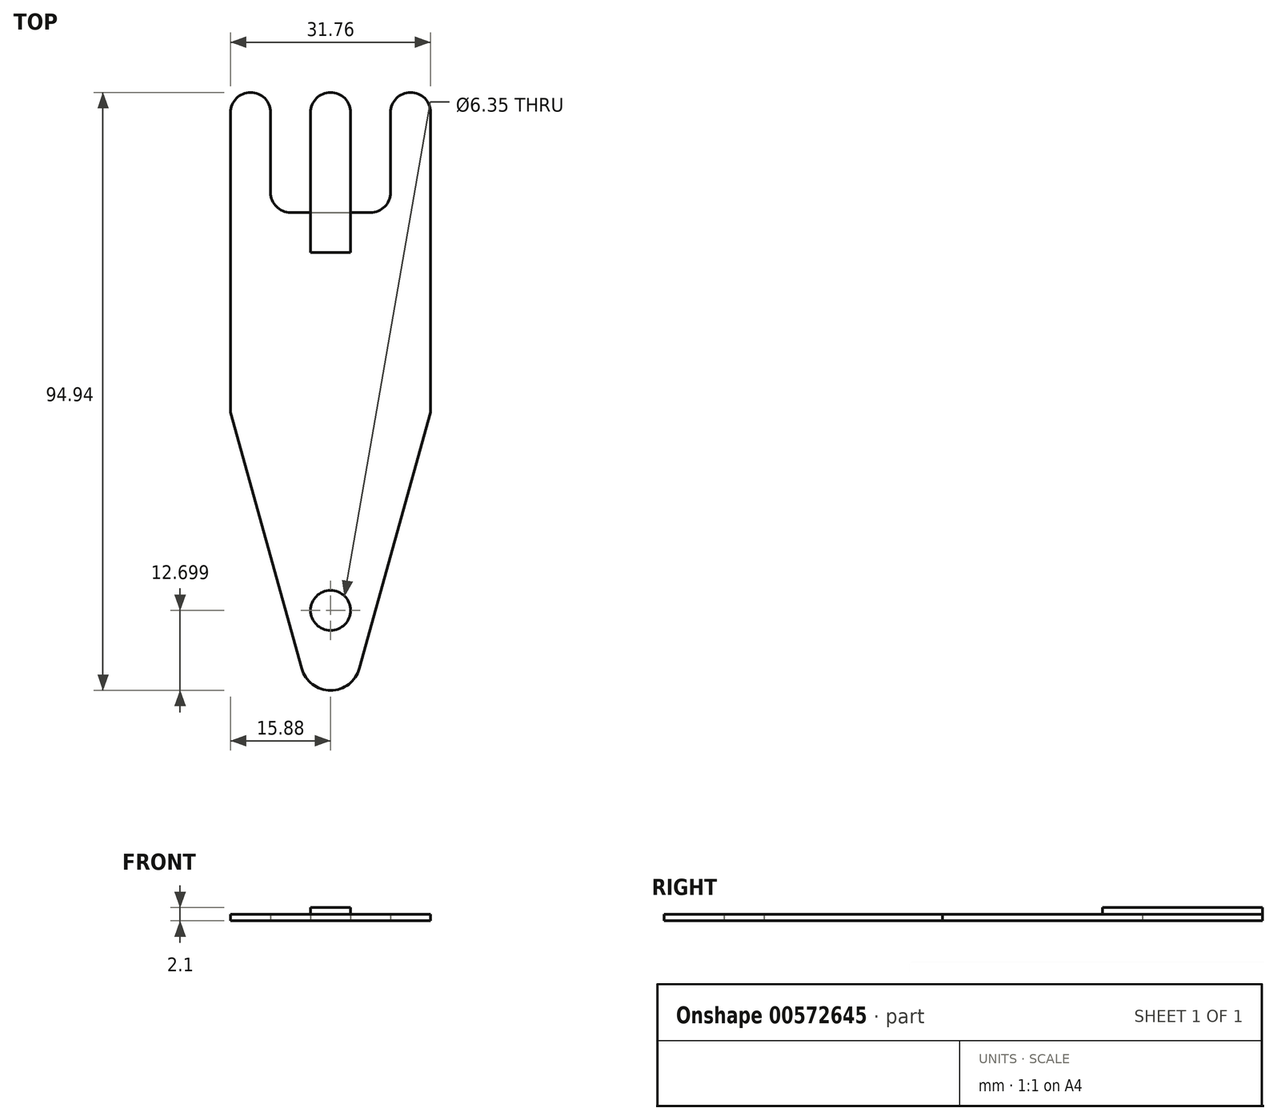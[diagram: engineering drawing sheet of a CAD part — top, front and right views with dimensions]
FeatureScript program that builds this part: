
annotation { "Feature Type Name" : "Feature", "Feature Type Description" : "" }
export const myFeature = defineFeature(function(context is Context, id is Id, definition is map)
    precondition{}
    {
        {
            var Q0;
            Q0=qCreatedBy(makeId("Top.planeOp"),FACE);
            var sketch = newSketch(context, id + "F0", { "sketchPlane" : qUnion([Q0])});
            skLineSegment(sketch, "E0.bottom", {"start": v(15.87, 0) * mm, "end": v(-15.88, 0) * mm});
            skLineSegment(sketch, "E0.top", {"start": v(15.87, 50.8) * mm, "end": v(-15.88, 50.8) * mm});
            skLineSegment(sketch, "E0.left", {"start": v(15.87, 0) * mm, "end": v(15.87, 50.8) * mm});
            skLineSegment(sketch, "E0.right", {"start": v(-15.88, 0) * mm, "end": v(-15.88, 50.8) * mm});
            skPoint(sketch, "E0.middle", {"position": v(0, 25.4) * mm});
            skLineSegment(sketch, "E1", {"start": v(-15.88, 0) * mm, "end": v(-4.59, -40.65) * mm});
            skLineSegment(sketch, "E2", {"start": v(4.59, -40.65) * mm, "end": v(15.87, 0) * mm});
            skPoint(sketch, "E3.visualSharp", {"position": v(0, -57.18) * mm});
            skArc(sketch, "E3.filletArc", {"start": v(-4.59, -40.65) * mm, "mid": v(0, -44.14) * mm, "end": v(4.59, -40.65) * mm});
            skLineSegment(sketch, "E4.bottom", {"start": v(-9.52, 50.8) * mm, "end": v(-3.17, 50.8) * mm});
            skLineSegment(sketch, "E4.top", {"start": v(-9.52, 31.75) * mm, "end": v(-3.17, 31.75) * mm});
            skLineSegment(sketch, "E4.left", {"start": v(-9.52, 50.8) * mm, "end": v(-9.52, 31.75) * mm});
            skLineSegment(sketch, "E4.right", {"start": v(-3.17, 50.8) * mm, "end": v(-3.17, 31.75) * mm});
            skLineSegment(sketch, "E5.bottom", {"start": v(3.17, 50.8) * mm, "end": v(9.52, 50.8) * mm});
            skLineSegment(sketch, "E5.top", {"start": v(3.17, 31.75) * mm, "end": v(9.52, 31.75) * mm});
            skLineSegment(sketch, "E5.left", {"start": v(3.17, 50.8) * mm, "end": v(3.17, 31.75) * mm});
            skLineSegment(sketch, "E5.right", {"start": v(9.52, 50.8) * mm, "end": v(9.52, 31.75) * mm});
            skSolve(sketch);
        }
        {
            var Q0;
            Q0=makeQuery(id+"F0.imprint","IMPRINT",FACE,{"disambiguationData":[TD([[makeQuery(id+"F0.imprint","IMPRINT",EDGE,{"derivedFrom":sQuery(id+"F0.wireOp",EDGE,"E0.bottom")}),-1.0]])]});
            var Q1;
            Q1=makeQuery(id+"F0.imprint","IMPRINT",FACE,{"disambiguationData":[TD([[makeQuery(id+"F0.imprint","IMPRINT",EDGE,{"derivedFrom":sQuery(id+"F0.wireOp",EDGE,"E0.bottom")}),1.0]])]});
            extrude(context, id + "F1", {"entities" : qUnion([Q0, Q1]), "depth" : 1.05 * mm, "offsetDistance" : 25.4 * mm});
        }
        {
            var Q0;
            Q0 = qSketchRegion(id + "F0", true);
            var sketch = newSketch(context, id + "F2", { "sketchPlane" : qUnion([Q0])});
            skCircle(sketch, "E6", {"center": v(0, -31.44) * mm, "radius": 3.18 * mm});
            skSolve(sketch);
        }
        {
            var Q0;
            Q0=makeQuery(id+"F2.imprint","IMPRINT",FACE,{"disambiguationData":[TD([[makeQuery(id+"F2.imprint","IMPRINT",EDGE,{"derivedFrom":sQuery(id+"F2.wireOp",EDGE,"E6")}),1.0]])]});
            extrude(context, id + "F3", {"entities" : qUnion([Q0]), "operationType" : NewBodyOperationType.REMOVE, "depth" : 28.17 * mm, "offsetDistance" : 25.4 * mm});
        }
        {
            var Q0;
            Q0=makeQuery(id+"F1.opExtrude","SWEPT_EDGE",EDGE,{"disambiguationData":[OSD([sQuery(id+"F0.wireOp",EDGE,"E0.top"),sQuery(id+"F0.wireOp",EDGE,"E0.left")])]});
            var Q1;
            Q1=makeQuery(id+"F1.opExtrude","SWEPT_EDGE",EDGE,{"disambiguationData":[OSD([sQuery(id+"F0.wireOp",EDGE,"E0.top"),sQuery(id+"F0.wireOp",EDGE,"E5.bottom"),sQuery(id+"F0.wireOp",EDGE,"E5.right")])]});
            var Q2;
            Q2=makeQuery(id+"F1.opExtrude","SWEPT_EDGE",EDGE,{"disambiguationData":[OSD([sQuery(id+"F0.wireOp",EDGE,"E0.top"),sQuery(id+"F0.wireOp",EDGE,"E5.bottom"),sQuery(id+"F0.wireOp",EDGE,"E5.left")])]});
            var Q3;
            Q3=makeQuery(id+"F1.opExtrude","SWEPT_EDGE",EDGE,{"disambiguationData":[OSD([sQuery(id+"F0.wireOp",EDGE,"E0.top"),sQuery(id+"F0.wireOp",EDGE,"E4.bottom"),sQuery(id+"F0.wireOp",EDGE,"E4.right")])]});
            var Q4;
            Q4=makeQuery(id+"F1.opExtrude","SWEPT_EDGE",EDGE,{"disambiguationData":[OSD([sQuery(id+"F0.wireOp",EDGE,"E0.top"),sQuery(id+"F0.wireOp",EDGE,"E4.bottom"),sQuery(id+"F0.wireOp",EDGE,"E4.left")])]});
            var Q5;
            Q5=makeQuery(id+"F1.opExtrude","SWEPT_EDGE",EDGE,{"disambiguationData":[OSD([sQuery(id+"F0.wireOp",EDGE,"E0.top"),sQuery(id+"F0.wireOp",EDGE,"E0.right")])]});
            fillet(context, id + "F4", {"entities" : qUnion([Q0, Q1, Q2, Q3, Q4, Q5]), "radius" : 3.17 * mm, "allowEdgeOverflow" : false});
        }
        {
            var Q0;
            Q0=makeQuery(id+"F1.opExtrude","CAP_FACE",FACE,{"disambiguationData":[OSD([sQuery(id+"F0.wireOp",EDGE,"E0.top"),sQuery(id+"F0.wireOp",EDGE,"E0.left"),sQuery(id+"F0.wireOp",EDGE,"E0.right"),sQuery(id+"F0.wireOp",EDGE,"E1"),sQuery(id+"F0.wireOp",EDGE,"E2"),sQuery(id+"F0.wireOp",EDGE,"E3.filletArc"),sQuery(id+"F0.wireOp",EDGE,"E4.top"),sQuery(id+"F0.wireOp",EDGE,"E4.left"),sQuery(id+"F0.wireOp",EDGE,"E4.right"),sQuery(id+"F0.wireOp",EDGE,"E5.top"),sQuery(id+"F0.wireOp",EDGE,"E5.left"),sQuery(id+"F0.wireOp",EDGE,"E5.right")])],"isStart":false});
            var sketch = newSketch(context, id + "F5", { "sketchPlane" : qUnion([Q0])});
            skLineSegment(sketch, "E7", {"start": v(-3.17, 31.75) * mm, "end": v(3.17, 31.75) * mm});
            skLineSegment(sketch, "E8.0", {"start": v(3.17, 47.63) * mm, "end": v(3.17, 31.75) * mm});
            skLineSegment(sketch, "E9.0", {"start": v(-3.17, 47.63) * mm, "end": v(-3.17, 31.75) * mm});
            skArc(sketch, "E10.0", {"start": v(3.18, 47.63) * mm, "mid": v(0, 50.8) * mm, "end": v(-3.17, 47.63) * mm});
            skSolve(sketch);
        }
        {
            var Q0;
            Q0 = qSketchRegion(id + "F5", true);
            extrude(context, id + "F6", {"entities" : qUnion([Q0]), "operationType" : NewBodyOperationType.ADD, "depth" : 1.05 * mm, "offsetDistance" : 25.4 * mm});
        }
        {
            var Q0;
            Q0=makeQuery(id+"F6.opExtrude","SWEPT_FACE",FACE,{"disambiguationData":[OSD([sQuery(id+"F5.wireOp",EDGE,"E7")])]});
            extrude(context, id + "F7", {"entities" : qUnion([Q0]), "operationType" : NewBodyOperationType.ADD, "depth" : 6.35 * mm, "offsetDistance" : 25.4 * mm});
        }
        {
            var Q0;
            Q0 = qSketchRegion(id + "F5", true);
            extrude(context, id + "F8", {"entities" : qUnion([Q0]), "operationType" : NewBodyOperationType.REMOVE, "oppositeDirection" : true, "depth" : 1.05 * mm, "offsetDistance" : 25.4 * mm});
        }
        {
            var Q0;
            Q0=makeQuery(id+"F1.opExtrude","SWEPT_EDGE",EDGE,{"disambiguationData":[OSD([sQuery(id+"F0.wireOp",EDGE,"E4.top"),sQuery(id+"F0.wireOp",EDGE,"E4.left")])]});
            var Q1;
            Q1=makeQuery(id+"F1.opExtrude","SWEPT_EDGE",EDGE,{"disambiguationData":[OSD([sQuery(id+"F0.wireOp",EDGE,"E5.top"),sQuery(id+"F0.wireOp",EDGE,"E5.right")])]});
            fillet(context, id + "F9", {"entities" : qUnion([Q0, Q1]), "radius" : 3.17 * mm, "tangentPropagation" : true, "allowEdgeOverflow" : false});
        }
    });
